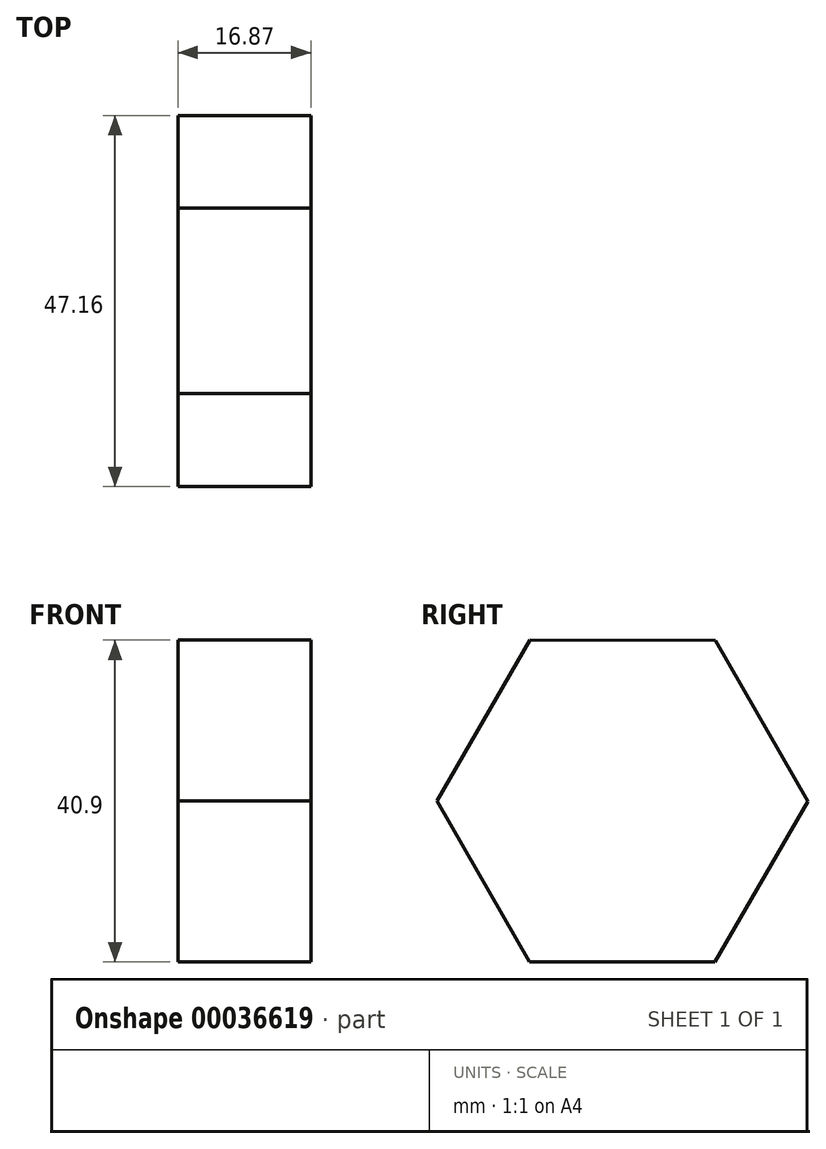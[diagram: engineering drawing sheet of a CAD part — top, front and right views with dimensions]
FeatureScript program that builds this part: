
annotation { "Feature Type Name" : "Feature", "Feature Type Description" : "" }
export const myFeature = defineFeature(function(context is Context, id is Id, definition is map)
    precondition{}
    {
        {
            var Q0;
            Q0=qCreatedBy(makeId("Right.planeOp"),FACE);
            var sketch = newSketch(context, id + "F0", { "sketchPlane" : qUnion([Q0])});
            skCircle(sketch, "E0", {"center": v(0, 0) * mm, "radius": 20.42 * mm});
            skCircle(sketch, "E1.cCircle", {"center": v(0, 0) * mm, "radius": 20.42 * mm, "construction": true});
            skLineSegment(sketch, "E1.0", {"start": v(11.84, 20.4) * mm, "end": v(23.58, -0.06) * mm});
            skLineSegment(sketch, "E1.1", {"start": v(23.58, -0.06) * mm, "end": v(11.74, -20.45) * mm});
            skLineSegment(sketch, "E1.2", {"start": v(11.74, -20.45) * mm, "end": v(-11.84, -20.4) * mm});
            skLineSegment(sketch, "E1.3", {"start": v(-11.84, -20.4) * mm, "end": v(-23.58, 0.06) * mm});
            skLineSegment(sketch, "E1.4", {"start": v(-23.58, 0.06) * mm, "end": v(-11.74, 20.45) * mm});
            skLineSegment(sketch, "E1.5", {"start": v(-11.74, 20.45) * mm, "end": v(11.84, 20.4) * mm});
            skPoint(sketch, "E1.0.midPoint", {"position": v(17.7, 10.17) * mm});
            skCircle(sketch, "E2", {"center": v(0, 0) * mm, "radius": 12.1 * mm});
            skSolve(sketch);
        }
        {
            var Q0;
            Q0=sQuery(id+"F0.wireOp",EDGE,"E1.5");
            var Q1;
            Q1=sQuery(id+"F0.wireOp",EDGE,"E1.3");
            var Q2;
            Q2=sQuery(id+"F0.wireOp",EDGE,"E1.4");
            var Q3;
            Q3=sQuery(id+"F0.wireOp",EDGE,"E1.0");
            var Q4;
            Q4=sQuery(id+"F0.wireOp",EDGE,"E1.1");
            var Q5;
            Q5=sQuery(id+"F0.wireOp",EDGE,"E1.2");
            extrude(context, id + "F1", {"bodyType" : ToolBodyType.SURFACE, "surfaceEntities" : qUnion([Q0, Q1, Q2, Q3, Q4, Q5]), "depth" : 16.87 * mm});
        }
    });
